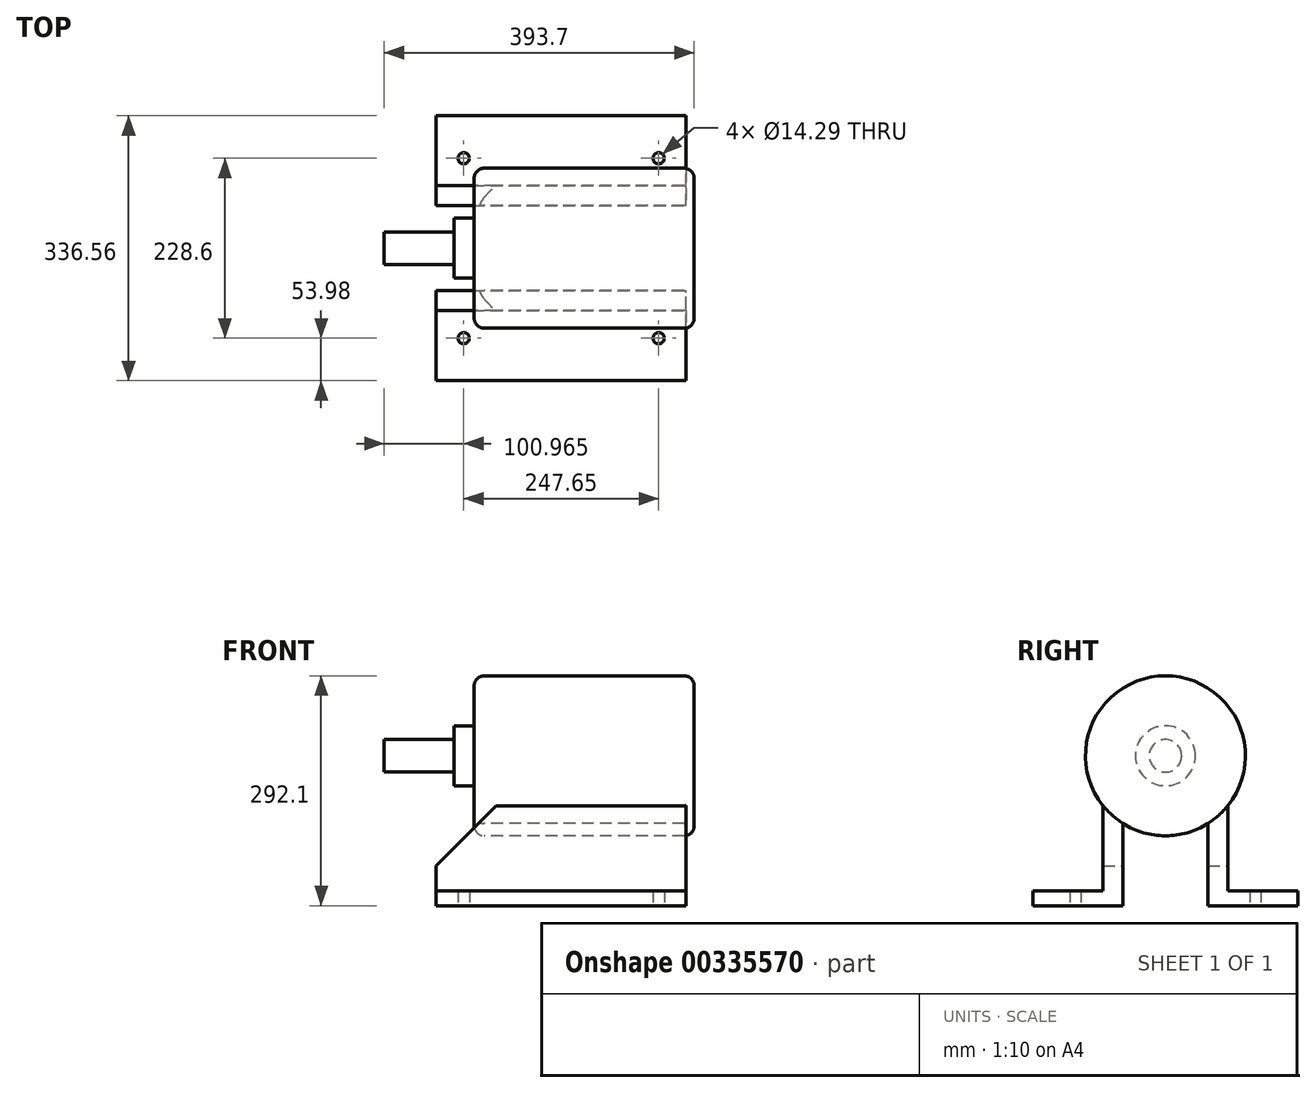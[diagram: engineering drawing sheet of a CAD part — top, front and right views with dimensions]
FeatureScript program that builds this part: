
annotation { "Feature Type Name" : "Feature", "Feature Type Description" : "" }
export const myFeature = defineFeature(function(context is Context, id is Id, definition is map)
    precondition{}
    {
        {
            var Q0;
            Q0=qCreatedBy(makeId("Right.planeOp"),FACE);
            var sketch = newSketch(context, id + "F0", { "sketchPlane" : qUnion([Q0])});
            skCircle(sketch, "E0", {"center": v(0, 0) * mm, "radius": 20.64 * mm});
            skSolve(sketch);
        }
        {
            var Q0;
            Q0=qSketchRegion(id+"F0",true);
            extrude(context, id + "F1", {"entities" : qUnion([Q0]), "depth" : 88.9 * mm});
        }
        {
            var Q0;
            Q0=makeQuery(id+"F1.opExtrude","CAP_FACE",FACE,{"disambiguationData":[OSD([sQuery(id+"F0.wireOp",EDGE,"E0")])],"isStart":false});
            var sketch = newSketch(context, id + "F2", { "sketchPlane" : qUnion([Q0])});
            skCircle(sketch, "E1", {"center": v(0, 0) * mm, "radius": 38.1 * mm});
            skSolve(sketch);
        }
        {
            var Q0;
            Q0=qSketchRegion(id+"F2",true);
            extrude(context, id + "F3", {"entities" : qUnion([Q0]), "operationType" : NewBodyOperationType.ADD, "depth" : 25.4 * mm});
        }
        {
            var Q0;
            Q0=makeQuery(id+"F3.opExtrude","CAP_FACE",FACE,{"disambiguationData":[OSD([sQuery(id+"F2.wireOp",EDGE,"E1")])],"isStart":false});
            var sketch = newSketch(context, id + "F4", { "sketchPlane" : qUnion([Q0])});
            skCircle(sketch, "E2", {"center": v(0, 0) * mm, "radius": 101.6 * mm});
            skSolve(sketch);
        }
        {
            var Q0;
            Q0=qSketchRegion(id+"F4",true);
            extrude(context, id + "F5", {"entities" : qUnion([Q0]), "operationType" : NewBodyOperationType.ADD, "depth" : 279.4 * mm});
        }
        {
            var Q0;
            Q0=qCreatedBy(makeId("Top.planeOp"),FACE);
            cPlane(context, id + "F6", {"entities" : qUnion([Q0]), "cplaneType" : CPlaneType.OFFSET, "offset" : 190.5 * mm, "oppositeDirection" : true, "width" : 152.4 * mm, "height" : 152.4 * mm});
        }
        {
            var Q0;
            Q0=qCreatedBy(id+"F6.planeOp",FACE);
            var sketch = newSketch(context, id + "F7", { "sketchPlane" : qUnion([Q0])});
            skLineSegment(sketch, "E3.0", {"start": v(114.3, 101.6) * mm, "end": v(114.3, -101.6) * mm, "construction": true});
            skLineSegment(sketch, "E4.0", {"start": v(66.04, 152.4) * mm, "end": v(66.04, -152.4) * mm, "construction": true});
            skLineSegment(sketch, "E5", {"start": v(-304.03, 0) * mm, "end": v(550.53, 0) * mm, "construction": true});
            skLineSegment(sketch, "E6.0", {"start": v(-304.03, -79.38) * mm, "end": v(550.53, -79.38) * mm, "construction": true});
            skLineSegment(sketch, "E7.bottom", {"start": v(66.04, -79.38) * mm, "end": v(383.54, -79.38) * mm});
            skLineSegment(sketch, "E7.top", {"start": v(66.04, -168.28) * mm, "end": v(383.54, -168.28) * mm});
            skLineSegment(sketch, "E7.left", {"start": v(66.04, -79.38) * mm, "end": v(66.04, -168.28) * mm});
            skLineSegment(sketch, "E7.right", {"start": v(383.54, -79.38) * mm, "end": v(383.54, -168.28) * mm});
            skLineSegment(sketch, "E8.MirrorCS", {"start": v(383.54, 79.38) * mm, "end": v(383.54, 168.28) * mm});
            skLineSegment(sketch, "E9.MirrorCS", {"start": v(66.04, 79.38) * mm, "end": v(66.04, 168.28) * mm});
            skLineSegment(sketch, "E10.MirrorCS", {"start": v(66.04, 79.38) * mm, "end": v(383.54, 79.38) * mm});
            skLineSegment(sketch, "E11.MirrorCS", {"start": v(66.04, 168.28) * mm, "end": v(383.54, 168.28) * mm});
            skSolve(sketch);
        }
        {
            var Q0;
            Q0=qSketchRegion(id+"F7",true);
            extrude(context, id + "F8", {"entities" : qUnion([Q0]), "depth" : 19.05 * mm});
        }
        {
            var Q0;
            Q0=makeQuery(id+"F8.opExtrude","CAP_FACE",FACE,{"disambiguationData":[OSD([sQuery(id+"F7.wireOp",EDGE,"E7.bottom"),sQuery(id+"F7.wireOp",EDGE,"E7.top"),sQuery(id+"F7.wireOp",EDGE,"E7.left"),sQuery(id+"F7.wireOp",EDGE,"E7.right")])],"isStart":true});
            var sketch = newSketch(context, id + "F9", { "sketchPlane" : qUnion([Q0])});
            skLineSegment(sketch, "E12", {"start": v(-240.84, 0) * mm, "end": v(606.88, 0) * mm, "construction": true});
            skLineSegment(sketch, "E13.0", {"start": v(-240.84, 114.3) * mm, "end": v(606.88, 114.3) * mm, "construction": true});
            skLineSegment(sketch, "E14.0", {"start": v(66.04, 168.28) * mm, "end": v(383.54, 168.28) * mm, "construction": true});
            skLineSegment(sketch, "E15", {"start": v(224.79, 168.28) * mm, "end": v(224.79, 79.38) * mm, "construction": true});
            skLineSegment(sketch, "E16.0", {"start": v(100.96, 168.28) * mm, "end": v(100.96, 79.38) * mm, "construction": true});
            skLineSegment(sketch, "E17.MirrorCS", {"start": v(348.62, 168.28) * mm, "end": v(348.62, 79.38) * mm, "construction": true});
            skPoint(sketch, "E18", {"position": v(100.96, 114.3) * mm});
            skPoint(sketch, "E19", {"position": v(348.62, 114.3) * mm});
            skPoint(sketch, "E20.MirrorP", {"position": v(100.96, -114.3) * mm});
            skPoint(sketch, "E21.MirrorP", {"position": v(348.62, -114.3) * mm});
            skSolve(sketch);
        }
        {
            var Q0;
            Q0=sQuery(id+"F9.wireOp",VERTEX,"E18");
            var Q1;
            Q1=sQuery(id+"F9.wireOp",VERTEX,"E19");
            var Q2;
            Q2=sQuery(id+"F9.wireOp",VERTEX,"E20.MirrorP");
            var Q3;
            Q3=sQuery(id+"F9.wireOp",VERTEX,"E21.MirrorP");
            var Q4;
            Q4=makeQuery(id+"F1.opExtrude","SWEPT_BODY",BODY,{"disambiguationData":[OSD([sQuery(id+"F0.wireOp",EDGE,"E0")])]});
            var Q5;
            Q5=makeQuery(id+"F8.opExtrude","SWEPT_BODY",BODY,{"disambiguationData":[OSD([sQuery(id+"F7.wireOp",EDGE,"E7.bottom"),sQuery(id+"F7.wireOp",EDGE,"E7.top"),sQuery(id+"F7.wireOp",EDGE,"E7.left"),sQuery(id+"F7.wireOp",EDGE,"E7.right")])]});
            var Q6;
            Q6=makeQuery(id+"F8.opExtrude","SWEPT_BODY",BODY,{"disambiguationData":[OSD([sQuery(id+"F7.wireOp",EDGE,"E8.MirrorCS"),sQuery(id+"F7.wireOp",EDGE,"E9.MirrorCS"),sQuery(id+"F7.wireOp",EDGE,"E10.MirrorCS"),sQuery(id+"F7.wireOp",EDGE,"E11.MirrorCS")])]});
            hole(context, id + "F10", {"style" : HoleStyle.SIMPLE, "endStyle" : HoleEndStyle.BLIND, "holeDiameter" : 14.29 * mm, "holeDepth" : 25.4 * mm, "tappedDepth" : 19.53 * mm, "tapClearance" : 3, "locations" : qUnion([Q0, Q1, Q2, Q3]), "scope" : qUnion([Q4, Q5, Q6])});
        }
        {
            var Q0;
            Q0=makeQuery(id+"F8.opExtrude","CAP_FACE",FACE,{"disambiguationData":[OSD([sQuery(id+"F7.wireOp",EDGE,"E7.bottom"),sQuery(id+"F7.wireOp",EDGE,"E7.top"),sQuery(id+"F7.wireOp",EDGE,"E7.left"),sQuery(id+"F7.wireOp",EDGE,"E7.right")])],"isStart":true});
            var sketch = newSketch(context, id + "F11", { "sketchPlane" : qUnion([Q0])});
            skLineSegment(sketch, "E22.bottom", {"start": v(66.04, 79.38) * mm, "end": v(383.54, 79.38) * mm});
            skLineSegment(sketch, "E22.top", {"start": v(66.04, 53.97) * mm, "end": v(383.54, 53.97) * mm});
            skLineSegment(sketch, "E22.left", {"start": v(66.04, 79.38) * mm, "end": v(66.04, 53.97) * mm});
            skLineSegment(sketch, "E22.right", {"start": v(383.54, 79.38) * mm, "end": v(383.54, 53.97) * mm});
            skLineSegment(sketch, "E23", {"start": v(-185.18, 0) * mm, "end": v(512.69, 0) * mm, "construction": true});
            skLineSegment(sketch, "E24.MirrorCS", {"start": v(383.54, -79.38) * mm, "end": v(383.54, -53.97) * mm});
            skLineSegment(sketch, "E25.MirrorCS", {"start": v(66.04, -79.38) * mm, "end": v(66.04, -53.97) * mm});
            skLineSegment(sketch, "E26.MirrorCS", {"start": v(66.04, -53.97) * mm, "end": v(383.54, -53.97) * mm});
            skLineSegment(sketch, "E27.MirrorCS", {"start": v(66.04, -79.38) * mm, "end": v(383.54, -79.38) * mm});
            skSolve(sketch);
        }
        {
            var Q0;
            Q0=qSketchRegion(id+"F11",true);
            extrude(context, id + "F12", {"entities" : qUnion([Q0]), "oppositeDirection" : true, "depth" : 152.4 * mm});
        }
        {
            var Q0;
            Q0=makeQuery(id+"F12.opExtrude","CAP_EDGE",EDGE,{"disambiguationData":[OSD([sQuery(id+"F11.wireOp",EDGE,"E22.left")])],"isStart":false});
            var Q1;
            Q1=makeQuery(id+"F12.opExtrude","CAP_EDGE",EDGE,{"disambiguationData":[OSD([sQuery(id+"F11.wireOp",EDGE,"E25.MirrorCS")])],"isStart":false});
            chamfer(context, id + "F13", {"entities" : qUnion([Q0, Q1]), "width" : 101.6 * mm, "tangentPropagation" : true});
        }
        {
            var Q0;
            Q0=makeQuery(id+"F1.opExtrude","SWEPT_BODY",BODY,{"disambiguationData":[OSD([sQuery(id+"F0.wireOp",EDGE,"E0")])]});
            var Q1;
            Q1=makeQuery(id+"F12.opExtrude","SWEPT_BODY",BODY,{"disambiguationData":[OSD([sQuery(id+"F11.wireOp",EDGE,"E22.bottom"),sQuery(id+"F11.wireOp",EDGE,"E22.top"),sQuery(id+"F11.wireOp",EDGE,"E22.left"),sQuery(id+"F11.wireOp",EDGE,"E22.right")])]});
            var Q2;
            Q2=makeQuery(id+"F8.opExtrude","SWEPT_BODY",BODY,{"disambiguationData":[OSD([sQuery(id+"F7.wireOp",EDGE,"E7.bottom"),sQuery(id+"F7.wireOp",EDGE,"E7.top"),sQuery(id+"F7.wireOp",EDGE,"E7.left"),sQuery(id+"F7.wireOp",EDGE,"E7.right")])]});
            var Q3;
            Q3=makeQuery(id+"F12.opExtrude","SWEPT_BODY",BODY,{"disambiguationData":[OSD([sQuery(id+"F11.wireOp",EDGE,"E24.MirrorCS"),sQuery(id+"F11.wireOp",EDGE,"E25.MirrorCS"),sQuery(id+"F11.wireOp",EDGE,"E26.MirrorCS"),sQuery(id+"F11.wireOp",EDGE,"E27.MirrorCS")])]});
            var Q4;
            Q4=makeQuery(id+"F8.opExtrude","SWEPT_BODY",BODY,{"disambiguationData":[OSD([sQuery(id+"F7.wireOp",EDGE,"E8.MirrorCS"),sQuery(id+"F7.wireOp",EDGE,"E9.MirrorCS"),sQuery(id+"F7.wireOp",EDGE,"E10.MirrorCS"),sQuery(id+"F7.wireOp",EDGE,"E11.MirrorCS")])]});
            booleanBodies(context, id + "F14", {"operationType" : BooleanOperationType.UNION, "tools" : qUnion([Q0, Q1, Q2, Q3, Q4])});
        }
        {
            var Q0;
            {var subQ0=sQuery(id+"F4.wireOp",EDGE,"E2");Q0=makeQuery(id+"F14.opBoolean","SPLIT",EDGE,{"disambiguationData":[TD([makeQuery(id+"F12.opExtrude","SWEPT_FACE",FACE,{"disambiguationData":[OSD([sQuery(id+"F11.wireOp",EDGE,"E22.bottom")])]})])],"derivedFrom":makeQuery(id+"F5.opExtrude","CAP_EDGE",EDGE,{"disambiguationData":[OSD([subQ0])],"isStart":true})});}
            var Q1;
            Q1=makeQuery(id+"F5.opExtrude","CAP_EDGE",EDGE,{"disambiguationData":[OSD([sQuery(id+"F4.wireOp",EDGE,"E2")])],"isStart":false});
            fillet(context, id + "F15", {"entities" : qUnion([Q0, Q1]), "radius" : 12.7 * mm, "allowEdgeOverflow" : false});
        }
    });
